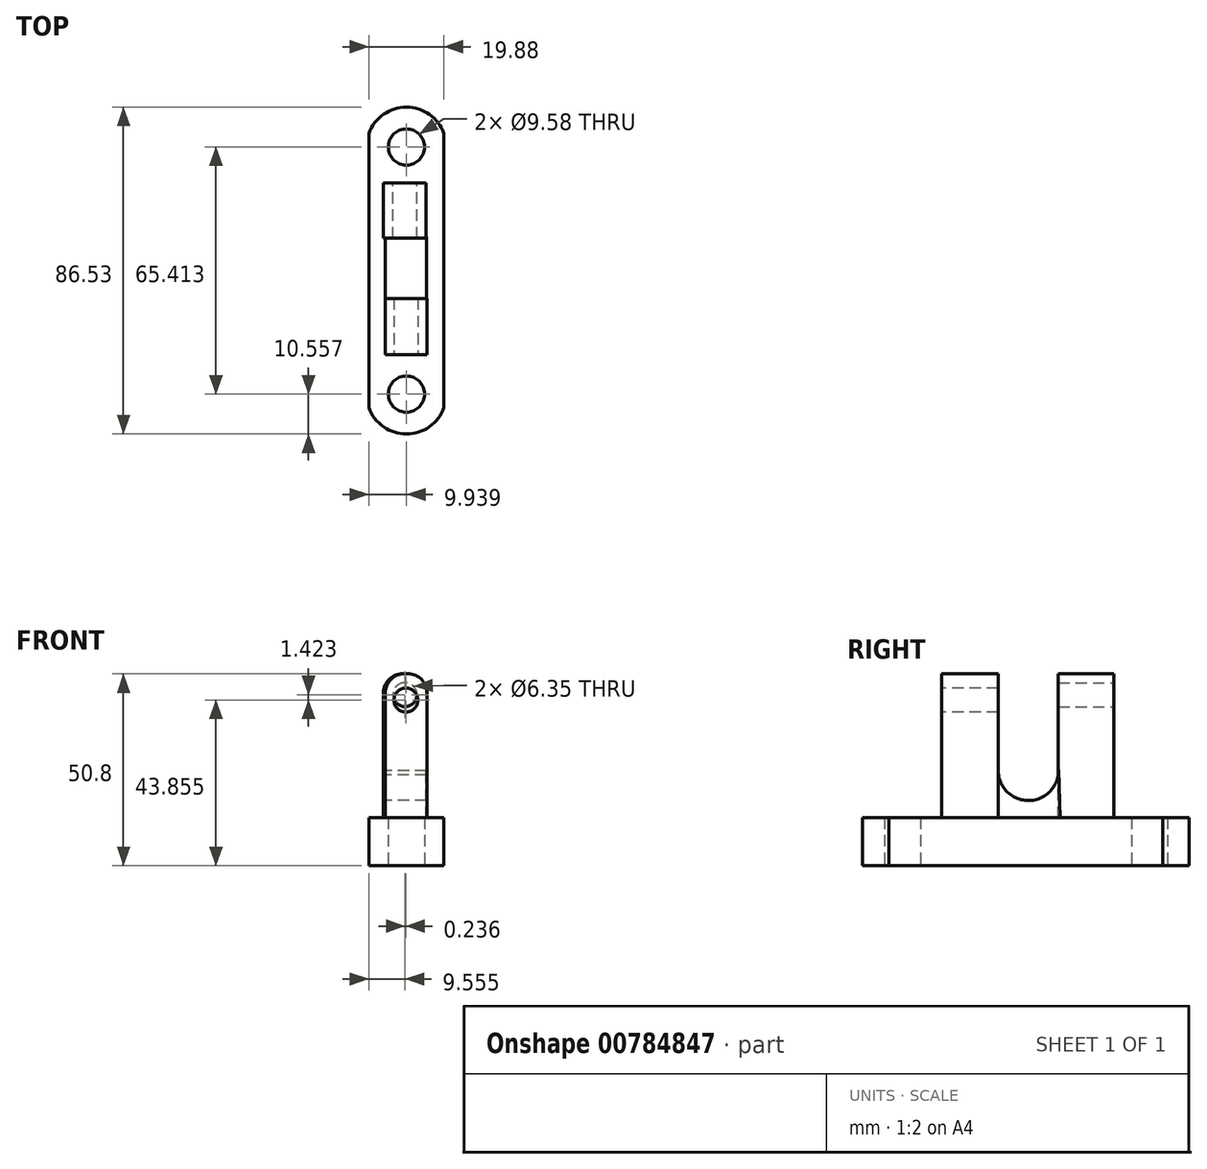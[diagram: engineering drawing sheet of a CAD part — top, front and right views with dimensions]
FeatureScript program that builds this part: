
annotation { "Feature Type Name" : "Feature", "Feature Type Description" : "" }
export const myFeature = defineFeature(function(context is Context, id is Id, definition is map)
    precondition{}
    {
        {
            var Q0;
            Q0=qCreatedBy(makeId("Top.planeOp"),FACE);
            var sketch = newSketch(context, id + "F0", { "sketchPlane" : qUnion([Q0])});
            skLineSegment(sketch, "E0", {"start": v(-19.88, 32.41) * mm, "end": v(-19.88, -40.13) * mm});
            skArc(sketch, "E1", {"start": v(0, 32.41) * mm, "mid": v(-9.94, 39.41) * mm, "end": v(-19.88, 32.41) * mm});
            skArc(sketch, "E2", {"start": v(-19.88, -40.13) * mm, "mid": v(-9.94, -47.12) * mm, "end": v(0, -40.13) * mm});
            skLineSegment(sketch, "E3", {"start": v(0, 32.41) * mm, "end": v(0, -40.13) * mm});
            skCircle(sketch, "E4", {"center": v(-9.94, 28.85) * mm, "radius": 4.79 * mm});
            skCircle(sketch, "E5", {"center": v(-9.94, -36.56) * mm, "radius": 4.79 * mm});
            skSolve(sketch);
        }
        {
            var Q0;
            Q0=makeQuery(id+"F0.imprint","IMPRINT",FACE,{"disambiguationData":[TD([[makeQuery(id+"F0.imprint","IMPRINT",EDGE,{"derivedFrom":sQuery(id+"F0.wireOp",EDGE,"E0")}),1.0]])]});
            extrude(context, id + "F1", {"entities" : qUnion([Q0]), "depth" : 12.7 * mm, "offsetDistance" : 25.4 * mm});
        }
        {
            var Q0;
            Q0=makeQuery(id+"F1.opExtrude","CAP_FACE",FACE,{"disambiguationData":[OSD([sQuery(id+"F0.wireOp",EDGE,"E0"),sQuery(id+"F0.wireOp",EDGE,"E1"),sQuery(id+"F0.wireOp",EDGE,"E2"),sQuery(id+"F0.wireOp",EDGE,"E3"),sQuery(id+"F0.wireOp",EDGE,"E4"),sQuery(id+"F0.wireOp",EDGE,"E5")])],"isStart":false});
            var sketch = newSketch(context, id + "F2", { "sketchPlane" : qUnion([Q0])});
            skLineSegment(sketch, "E6.bottom", {"start": v(-15.54, -26.15) * mm, "end": v(-4.46, -26.15) * mm});
            skLineSegment(sketch, "E6.top", {"start": v(-15.54, -11.2) * mm, "end": v(-4.46, -11.2) * mm});
            skLineSegment(sketch, "E6.left", {"start": v(-15.54, -26.15) * mm, "end": v(-15.54, -11.2) * mm});
            skLineSegment(sketch, "E6.right", {"start": v(-4.46, -26.15) * mm, "end": v(-4.46, -11.2) * mm});
            skSolve(sketch);
        }
        {
            var Q0;
            Q0=makeQuery(id+"F2.imprint","IMPRINT",FACE,{"disambiguationData":[TD([[makeQuery(id+"F2.imprint","IMPRINT",EDGE,{"derivedFrom":sQuery(id+"F2.wireOp",EDGE,"E6.bottom")}),1.0]])]});
            extrude(context, id + "F3", {"entities" : qUnion([Q0]), "operationType" : NewBodyOperationType.ADD, "depth" : 38.1 * mm, "offsetDistance" : 25.4 * mm});
        }
        {
            var Q0;
            Q0=makeQuery(id+"F3.opExtrude","SWEPT_FACE",FACE,{"disambiguationData":[OSD([sQuery(id+"F2.wireOp",EDGE,"E6.bottom")])]});
            var sketch = newSketch(context, id + "F4", { "sketchPlane" : qUnion([Q0])});
            skCircle(sketch, "E7", {"center": v(-10.09, 43.85) * mm, "radius": 3.52 * mm});
            skSolve(sketch);
        }
        {
            var Q0;
            Q0=sQuery(id+"F4.wireOp",VERTEX,"E7.center");
            var Q1;
            Q1=makeQuery(id+"F1.opExtrude","SWEPT_BODY",BODY,{"disambiguationData":[OSD([sQuery(id+"F0.wireOp",EDGE,"E0"),sQuery(id+"F0.wireOp",EDGE,"E1"),sQuery(id+"F0.wireOp",EDGE,"E2"),sQuery(id+"F0.wireOp",EDGE,"E3"),sQuery(id+"F0.wireOp",EDGE,"E4"),sQuery(id+"F0.wireOp",EDGE,"E5")])]});
            hole(context, id + "F5", {"style" : HoleStyle.SIMPLE, "endStyle" : HoleEndStyle.THROUGH, "holeDiameter" : 6.35 * mm, "majorDiameter" : 6.35 * mm, "isTappedThrough" : true, "tappedDepth" : 12.7 * mm, "tapClearance" : 3, "locations" : qUnion([Q0]), "scope" : qUnion([Q1])});
        }
        {
            var Q0;
            Q0=makeQuery(id+"F3.opExtrude","CAP_EDGE",EDGE,{"disambiguationData":[OSD([sQuery(id+"F2.wireOp",EDGE,"E6.right")])],"isStart":false});
            var Q1;
            Q1=makeQuery(id+"F3.opExtrude","CAP_EDGE",EDGE,{"disambiguationData":[OSD([sQuery(id+"F2.wireOp",EDGE,"E6.left")])],"isStart":false});
            fillet(context, id + "F6", {"entities" : qUnion([Q0, Q1]), "radius" : 5.08 * mm, "tangentPropagation" : true, "allowEdgeOverflow" : false});
        }
        {
            var Q0;
            Q0=makeQuery(id+"F1.opExtrude","CAP_FACE",FACE,{"disambiguationData":[OSD([sQuery(id+"F0.wireOp",EDGE,"E0"),sQuery(id+"F0.wireOp",EDGE,"E1"),sQuery(id+"F0.wireOp",EDGE,"E2"),sQuery(id+"F0.wireOp",EDGE,"E3"),sQuery(id+"F0.wireOp",EDGE,"E4"),sQuery(id+"F0.wireOp",EDGE,"E5")])],"isStart":false});
            var sketch = newSketch(context, id + "F7", { "sketchPlane" : qUnion([Q0])});
            skLineSegment(sketch, "E8", {"start": v(-19.88, 0) * mm, "end": v(0, 0) * mm});
            skSolve(sketch);
        }
        {
            var Q0;
            {var subQ2=sQuery(id+"F7.wireOp",EDGE,"E8");Q0=makeQuery(id+"F7.imprint","IMPRINT",FACE,{"disambiguationData":[TD([[makeQuery(id+"F7.imprint","IMPRINT",EDGE,{"derivedFrom":subQ2}),1.0]])]});}
            var sketch = newSketch(context, id + "F8", { "sketchPlane" : qUnion([Q0])});
            skLineSegment(sketch, "E9.bottom", {"start": v(-16.03, 19.4) * mm, "end": v(-4.7, 19.4) * mm});
            skLineSegment(sketch, "E9.top", {"start": v(-16.03, 4.7) * mm, "end": v(-4.7, 4.7) * mm});
            skLineSegment(sketch, "E9.left", {"start": v(-16.03, 19.4) * mm, "end": v(-16.03, 4.7) * mm});
            skLineSegment(sketch, "E9.right", {"start": v(-4.7, 19.4) * mm, "end": v(-4.7, 4.7) * mm});
            skSolve(sketch);
        }
        {
            var Q0;
            Q0=makeQuery(id+"F8.imprint","IMPRINT",FACE,{"disambiguationData":[TD([[makeQuery(id+"F8.imprint","IMPRINT",EDGE,{"derivedFrom":sQuery(id+"F8.wireOp",EDGE,"E9.bottom")}),-1.0]])]});
            extrude(context, id + "F9", {"entities" : qUnion([Q0]), "operationType" : NewBodyOperationType.ADD, "depth" : 38.1 * mm, "offsetDistance" : 25.4 * mm});
        }
        {
            var Q0;
            Q0=makeQuery(id+"F9.opExtrude","SWEPT_FACE",FACE,{"disambiguationData":[OSD([sQuery(id+"F8.wireOp",EDGE,"E9.bottom")])]});
            var sketch = newSketch(context, id + "F10", { "sketchPlane" : qUnion([Q0])});
            skCircle(sketch, "E10", {"center": v(10.32, 45.28) * mm, "radius": 3.01 * mm});
            skSolve(sketch);
        }
        {
            var Q0;
            Q0=sQuery(id+"F10.wireOp",VERTEX,"E10.center");
            var Q1;
            Q1=makeQuery(id+"F1.opExtrude","SWEPT_BODY",BODY,{"disambiguationData":[OSD([sQuery(id+"F0.wireOp",EDGE,"E0"),sQuery(id+"F0.wireOp",EDGE,"E1"),sQuery(id+"F0.wireOp",EDGE,"E2"),sQuery(id+"F0.wireOp",EDGE,"E3"),sQuery(id+"F0.wireOp",EDGE,"E4"),sQuery(id+"F0.wireOp",EDGE,"E5")])]});
            hole(context, id + "F11", {"style" : HoleStyle.SIMPLE, "endStyle" : HoleEndStyle.BLIND, "holeDiameter" : 6.35 * mm, "majorDiameter" : 6.35 * mm, "holeDepth" : 25.4 * mm, "isTappedThrough" : true, "tappedDepth" : 12.7 * mm, "tapClearance" : 3, "locations" : qUnion([Q0]), "scope" : qUnion([Q1])});
        }
        {
            var Q0;
            Q0=makeQuery(id+"F9.opExtrude","CAP_EDGE",EDGE,{"disambiguationData":[OSD([sQuery(id+"F8.wireOp",EDGE,"E9.right")])],"isStart":false});
            var Q1;
            Q1=makeQuery(id+"F9.opExtrude","CAP_EDGE",EDGE,{"disambiguationData":[OSD([sQuery(id+"F8.wireOp",EDGE,"E9.left")])],"isStart":false});
            fillet(context, id + "F12", {"entities" : qUnion([Q0, Q1]), "radius" : 5.08 * mm, "tangentPropagation" : true, "allowEdgeOverflow" : false});
        }
        {
            var Q0;
            Q0=makeQuery(id+"F3.opExtrude","SWEPT_FACE",FACE,{"disambiguationData":[OSD([sQuery(id+"F2.wireOp",EDGE,"E6.left")])]});
            var sketch = newSketch(context, id + "F13", { "sketchPlane" : qUnion([Q0])});
            skArc(sketch, "E11", {"start": v(-4.78, 25.48) * mm, "mid": v(3.16, 17.24) * mm, "end": v(11.2, 25.38) * mm});
            skLineSegment(sketch, "E12", {"start": v(-4.78, 25.48) * mm, "end": v(-5.19, 11.87) * mm});
            skLineSegment(sketch, "E13", {"start": v(-5.19, 11.87) * mm, "end": v(11.2, 12.7) * mm});
            skLineSegment(sketch, "E14", {"start": v(11.2, 12.7) * mm, "end": v(11.2, 25.38) * mm});
            skSolve(sketch);
        }
        {
            var Q0;
            Q0 = qSketchRegion(id + "F13", true);
            extrude(context, id + "F14", {"entities" : qUnion([Q0]), "operationType" : NewBodyOperationType.ADD, "oppositeDirection" : true, "depth" : 10.92 * mm, "offsetDistance" : 25.4 * mm});
        }
    });
